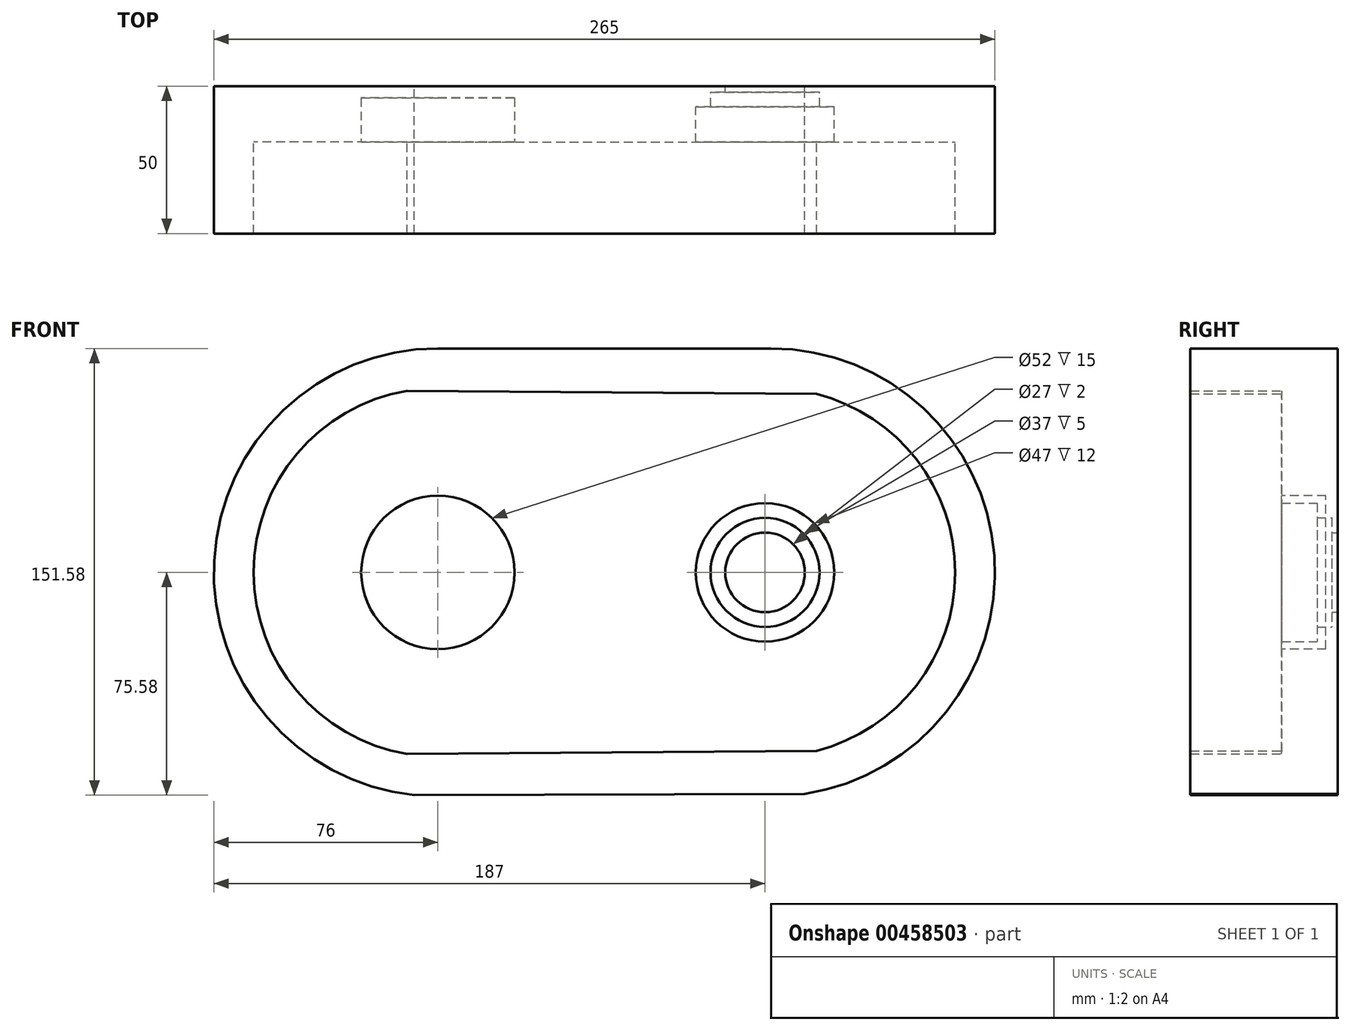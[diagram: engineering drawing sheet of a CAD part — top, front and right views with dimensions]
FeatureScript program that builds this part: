
annotation { "Feature Type Name" : "Feature", "Feature Type Description" : "" }
export const myFeature = defineFeature(function(context is Context, id is Id, definition is map)
    precondition{}
    {
        {
            var Q0;
            Q0=qCreatedBy(makeId("Front.planeOp"),FACE);
            var sketch = newSketch(context, id + "F0", { "sketchPlane" : qUnion([Q0])});
            skArc(sketch, "E0", {"start": v(8.5, -75.52) * mm, "mid": v(-0.26, 76) * mm, "end": v(-7.98, -75.58) * mm});
            skArc(sketch, "E1", {"start": v(124.44, -75.13) * mm, "mid": v(112.74, 76) * mm, "end": v(102.06, -75.2) * mm});
            skLineSegment(sketch, "E2", {"start": v(0, 76) * mm, "end": v(113, 76) * mm});
            skLineSegment(sketch, "E3", {"start": v(-7.98, -75.58) * mm, "end": v(124.44, -75.13) * mm});
            skSolve(sketch);
        }
        {
            var Q0;
            {var subQ1=sQuery(id+"F0.wireOp",EDGE,"E0");var subQ4=sQuery(id+"F0.wireOp",EDGE,"E3");var subQ7=makeQuery(id+"F0.imprint","INTERSECT",VERTEX,{"disambiguationData":[OD(0.0)],"derivedFrom":[subQ1,subQ4]});Q0=makeQuery(id+"F0.imprint","IMPRINT",FACE,{"disambiguationData":[TD([[makeQuery(id+"F0.imprint","IMPRINT",EDGE,{"disambiguationData":[TD([[subQ7,-1.0]])],"derivedFrom":subQ1}),1.0]])]});}
            var Q1;
            {var subQ0=sQuery(id+"F0.wireOp",EDGE,"E2");Q1=makeQuery(id+"F0.imprint","IMPRINT",FACE,{"disambiguationData":[TD([[makeQuery(id+"F0.imprint","IMPRINT",EDGE,{"derivedFrom":subQ0}),-1.0]])]});}
            var Q2;
            {var subQ1=sQuery(id+"F0.wireOp",EDGE,"E1");var subQ3=sQuery(id+"F0.wireOp",EDGE,"E0");var subQ4=makeQuery(id+"F0.imprint","INTERSECT",VERTEX,{"disambiguationData":[OD(0.0)],"derivedFrom":[subQ3,subQ1]});Q2=makeQuery(id+"F0.imprint","IMPRINT",FACE,{"disambiguationData":[TD([[makeQuery(id+"F0.imprint","IMPRINT",EDGE,{"disambiguationData":[TD([[subQ4,-1.0]])],"derivedFrom":subQ3}),-1.0]])]});}
            var Q3;
            {var subQ0=sQuery(id+"F0.wireOp",EDGE,"E1");var subQ1=sQuery(id+"F0.wireOp",EDGE,"E0");var subQ2=makeQuery(id+"F0.imprint","INTERSECT",VERTEX,{"disambiguationData":[OD(0.0)],"derivedFrom":[subQ1,subQ0]});Q3=makeQuery(id+"F0.imprint","IMPRINT",FACE,{"disambiguationData":[TD([[makeQuery(id+"F0.imprint","IMPRINT",EDGE,{"disambiguationData":[TD([[subQ2,-1.0]])],"derivedFrom":subQ1}),1.0]])]});}
            var Q4;
            {var subQ0=sQuery(id+"F0.wireOp",EDGE,"E3");var subQ1=sQuery(id+"F0.wireOp",EDGE,"E0");var subQ2=makeQuery(id+"F0.imprint","INTERSECT",VERTEX,{"disambiguationData":[OD(0.0)],"derivedFrom":[subQ1,subQ0]});Q4=makeQuery(id+"F0.imprint","IMPRINT",FACE,{"disambiguationData":[TD([[makeQuery(id+"F0.imprint","IMPRINT",EDGE,{"disambiguationData":[TD([[subQ2,-1.0]])],"derivedFrom":subQ1}),-1.0]])]});}
            extrude(context, id + "F1", {"entities" : qUnion([Q0, Q1, Q2, Q3, Q4]), "depth" : 50 * mm, "offsetDistance" : 25 * mm});
        }
        {
            var Q0;
            Q0=qCreatedBy(makeId("Front.planeOp"),FACE);
            cPlane(context, id + "F2", {"entities" : qUnion([Q0]), "cplaneType" : CPlaneType.OFFSET, "offset" : 19 * mm, "width" : 150 * mm, "height" : 150 * mm});
        }
        {
            var Q0;
            Q0=qCreatedBy(id+"F2.planeOp",FACE);
            var sketch = newSketch(context, id + "F3", { "sketchPlane" : qUnion([Q0])});
            skArc(sketch, "E4", {"start": v(-10.5, 61.61) * mm, "mid": v(-62.5, 0) * mm, "end": v(-10.5, -61.61) * mm});
            skArc(sketch, "E5", {"start": v(128.5, -60.55) * mm, "mid": v(175.5, 0) * mm, "end": v(128.5, 60.55) * mm});
            skLineSegment(sketch, "E6", {"start": v(-10.5, 61.61) * mm, "end": v(128.5, 60.55) * mm});
            skLineSegment(sketch, "E7.MirrorCS", {"start": v(-10.5, -61.61) * mm, "end": v(128.5, -60.55) * mm});
            skLineSegment(sketch, "E8", {"start": v(-10.5, -61.61) * mm, "end": v(-10.5, 61.61) * mm});
            skLineSegment(sketch, "E9", {"start": v(128.5, 60.55) * mm, "end": v(128.5, -60.55) * mm});
            skSolve(sketch);
        }
        {
            var Q0;
            Q0 = qSketchRegion(id + "F3", true);
            extrude(context, id + "F4", {"entities" : qUnion([Q0]), "operationType" : NewBodyOperationType.REMOVE, "depth" : 47 * mm});
        }
        {
            var Q0;
            Q0=qCreatedBy(id+"F2.planeOp",FACE);
            var sketch = newSketch(context, id + "F5", { "sketchPlane" : qUnion([Q0])});
            skCircle(sketch, "E10", {"center": v(0, 0) * mm, "radius": 26 * mm});
            skSolve(sketch);
        }
        {
            var Q0;
            Q0=makeQuery(id+"F5.imprint","IMPRINT",FACE,{"disambiguationData":[TD([[makeQuery(id+"F5.imprint","IMPRINT",EDGE,{"derivedFrom":sQuery(id+"F5.wireOp",EDGE,"E10")}),1.0]])]});
            extrude(context, id + "F6", {"entities" : qUnion([Q0]), "operationType" : NewBodyOperationType.REMOVE, "oppositeDirection" : true, "depth" : 15 * mm});
        }
        {
            var Q0;
            Q0=qCreatedBy(makeId("Right.planeOp"),FACE);
            cPlane(context, id + "F7", {"entities" : qUnion([Q0]), "cplaneType" : CPlaneType.OFFSET, "offset" : 111 * mm, "width" : 150 * mm, "height" : 150 * mm});
        }
        {
            var Q0;
            Q0=qCreatedBy(id+"F7.planeOp",FACE);
            var sketch = newSketch(context, id + "F8", { "sketchPlane" : qUnion([Q0])});
            skLineSegment(sketch, "E11", {"start": v(0, 0) * mm, "end": v(-50.92, 0) * mm, "construction": true});
            skLineSegment(sketch, "E12", {"start": v(0, 0) * mm, "end": v(-2, 0) * mm});
            skLineSegment(sketch, "E13", {"start": v(0, 13.5) * mm, "end": v(-2, 13.5) * mm});
            skLineSegment(sketch, "E14", {"start": v(-17, 0) * mm, "end": v(0, 0) * mm});
            skLineSegment(sketch, "E15", {"start": v(0, 13.5) * mm, "end": v(0, 13.5) * mm});
            skLineSegment(sketch, "E16", {"start": v(0, 13.5) * mm, "end": v(0, 0) * mm});
            skLineSegment(sketch, "E17", {"start": v(-2, 0) * mm, "end": v(-2, 13.5) * mm});
            skLineSegment(sketch, "E18", {"start": v(-2, 13.5) * mm, "end": v(-2, 18.5) * mm});
            skPoint(sketch, "E19.orphan", {"position": v(-5, 13.5) * mm});
            skLineSegment(sketch, "E20", {"start": v(-2, 18.5) * mm, "end": v(-7, 18.5) * mm});
            skLineSegment(sketch, "E21", {"start": v(-7, 18.5) * mm, "end": v(-7, 23.5) * mm});
            skLineSegment(sketch, "E22", {"start": v(-7, 23.5) * mm, "end": v(-19, 23.5) * mm});
            skLineSegment(sketch, "E23", {"start": v(-19, 23.5) * mm, "end": v(-19, 0) * mm});
            skLineSegment(sketch, "E24", {"start": v(-19, 0) * mm, "end": v(0, 0) * mm});
            skSolve(sketch);
        }
        {
            var Q0;
            Q0 = qSketchRegion(id + "F8", true);
            var Q1;
            Q1=sQuery(id+"F8.wireOp",EDGE,"E14");
            revolve(context, id + "F9", {"operationType" : NewBodyOperationType.REMOVE, "entities" : qUnion([Q0]), "axis" : qUnion([Q1]), "revolveType" : RevolveType.FULL, "oppositeDirection" : true});
        }
    });
